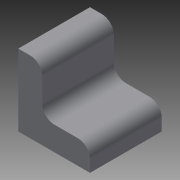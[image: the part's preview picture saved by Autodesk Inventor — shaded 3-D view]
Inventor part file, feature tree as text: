
AUTODESK INVENTOR PART (.ipt)
format: ipt  version: 2015 (Build 190159000, 159)  size: 93,696 bytes
history: native  units: in
note: dims shown in document units (in); Inventor stores cm internally (conversion verified against a paired STEP export)
features: fillet x3, extrude x2, sketch x2
ambient origin geometry x8: Origin, YZ Plane, XZ Plane, XY Plane, X Axis, Y Axis, Z Axis, Center Point
bodies: Solid1 (feature_tree)
feature tree (7):
  extrude  "Extrusion1"  Depth=1.5in
  extrude  "Extrusion2"  Depth=0.5in
  fillet  "Fillet1"  [1 undecoded]
  fillet  "Fillet2"  Radius=0.25in
  fillet  "Fillet3"  Radius=0.25in
  sketch  "Sketch1"  dims[d0=1.5in d1=1.5in]
  sketch  "Sketch2"  dims[d2=1.5in d3=0.0in d5=0.5in d8=0.0in d9=0.0in d10=0.25in d11=0.25in d12=0.25in]
note: 1 required parameter value undecoded (feature->parameter linkage not recoverable at this tier; creation-order binding heuristic only, values carry confidence <= 0.55)
